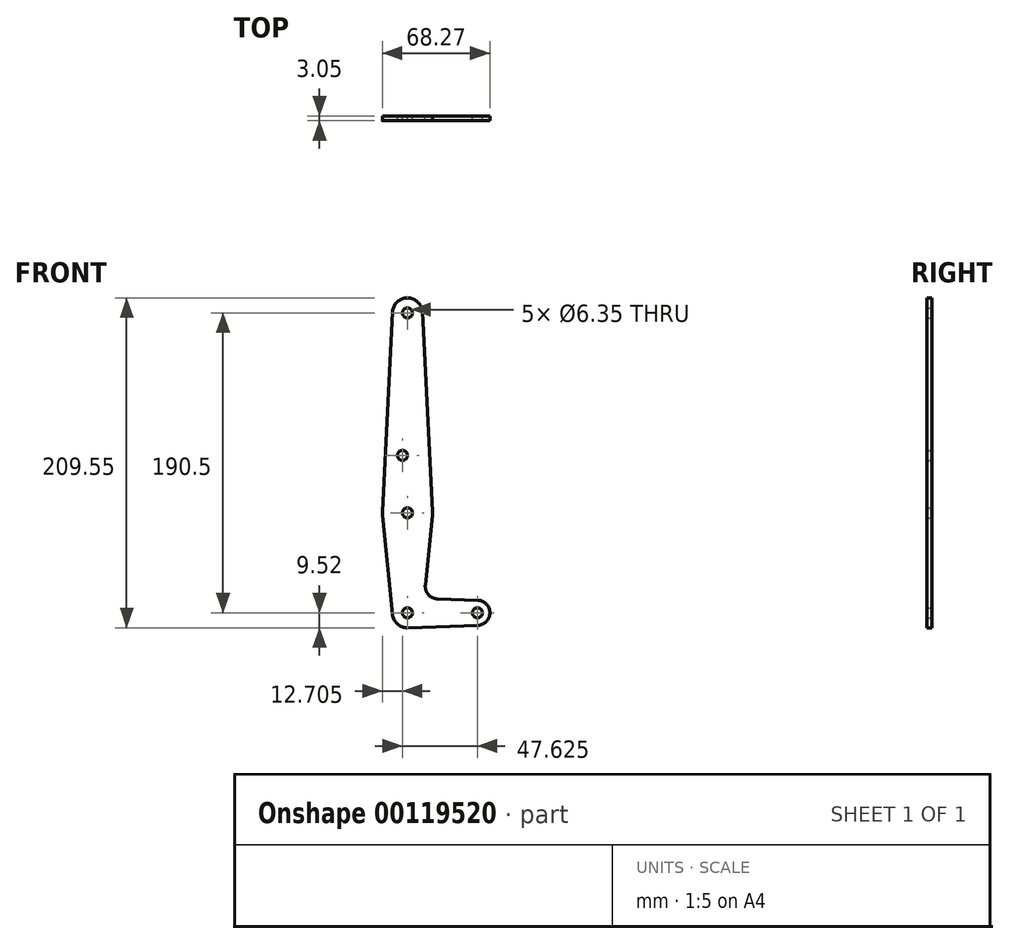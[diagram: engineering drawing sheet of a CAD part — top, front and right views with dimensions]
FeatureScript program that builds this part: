
annotation { "Feature Type Name" : "Feature", "Feature Type Description" : "" }
export const myFeature = defineFeature(function(context is Context, id is Id, definition is map)
    precondition{}
    {
        {
            var Q0;
            Q0=qCreatedBy(makeId("Front.planeOp"),FACE);
            var sketch = newSketch(context, id + "F0", { "sketchPlane" : qUnion([Q0])});
            skLineSegment(sketch, "E0", {"start": v(44.45, 0) * mm, "end": v(0, 0) * mm, "construction": true});
            skLineSegment(sketch, "E1", {"start": v(0, 0) * mm, "end": v(0, 190.5) * mm, "construction": true});
            skCircle(sketch, "E2", {"center": v(44.45, 0) * mm, "radius": 7.94 * mm});
            skCircle(sketch, "E3", {"center": v(0, 0) * mm, "radius": 9.53 * mm});
            skCircle(sketch, "E4", {"center": v(0, 63.5) * mm, "radius": 15.88 * mm});
            skCircle(sketch, "E5", {"center": v(0, 190.5) * mm, "radius": 9.53 * mm});
            skLineSegment(sketch, "E6", {"start": v(-9.48, -0.95) * mm, "end": v(-15.8, 61.91) * mm});
            skLineSegment(sketch, "E7", {"start": v(15.8, 61.91) * mm, "end": v(11.34, 17.6) * mm});
            skLineSegment(sketch, "E8", {"start": v(-15.86, 64.3) * mm, "end": v(-9.51, 190.98) * mm});
            skLineSegment(sketch, "E9", {"start": v(15.86, 64.3) * mm, "end": v(9.51, 190.98) * mm});
            skCircle(sketch, "E10", {"center": v(0, 190.5) * mm, "radius": 3.18 * mm});
            skCircle(sketch, "E11", {"center": v(0, 63.5) * mm, "radius": 3.18 * mm});
            skCircle(sketch, "E12", {"center": v(0, 0) * mm, "radius": 3.18 * mm});
            skCircle(sketch, "E13", {"center": v(44.45, 0) * mm, "radius": 3.18 * mm});
            skCircle(sketch, "E14", {"center": v(-3.18, 100.03) * mm, "radius": 3.18 * mm});
            skLineSegment(sketch, "E15", {"start": v(0.34, -9.52) * mm, "end": v(44.73, -7.93) * mm});
            skLineSegment(sketch, "E16", {"start": v(44.73, 7.93) * mm, "end": v(18.97, 8.85) * mm});
            skArc(sketch, "E17.filletArc", {"start": v(11.34, 17.6) * mm, "mid": v(13.26, 11.57) * mm, "end": v(18.97, 8.85) * mm});
            skSolve(sketch);
        }
        {
            var Q0;
            Q0=qSketchRegion(id+"F0",true);
            extrude(context, id + "F1", {"entities" : qUnion([Q0]), "depth" : 3.05 * mm});
        }
    });
